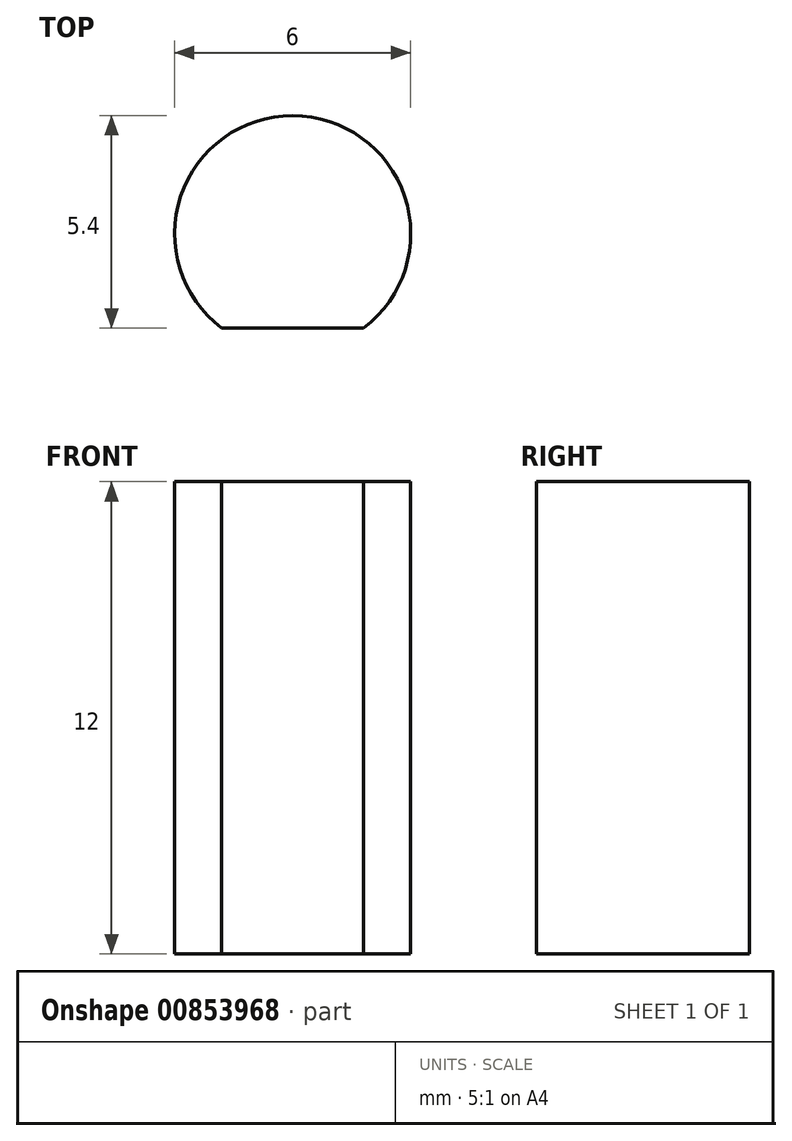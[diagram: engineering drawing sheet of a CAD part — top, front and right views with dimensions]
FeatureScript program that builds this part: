
annotation { "Feature Type Name" : "Feature", "Feature Type Description" : "" }
export const myFeature = defineFeature(function(context is Context, id is Id, definition is map)
    precondition{}
    {
        {
            var Q0;
            Q0=qCreatedBy(makeId("Top.planeOp"),FACE);
            var sketch = newSketch(context, id + "F0", { "sketchPlane" : qUnion([Q0])});
            skCircle(sketch, "E0", {"center": v(0, 0) * mm, "radius": 6.35 * mm});
            skSolve(sketch);
        }
        {
            var Q0;
            Q0=makeQuery(id+"F0.imprint","IMPRINT",FACE,{"disambiguationData":[TD([[makeQuery(id+"F0.imprint","IMPRINT",EDGE,{"derivedFrom":sQuery(id+"F0.wireOp",EDGE,"E0")}),1.0]])]});
            extrude(context, id + "F1", {"entities" : qUnion([Q0]), "depth" : 12 * mm, "offsetDistance" : 25 * mm});
        }
        {
            var Q0;
            Q0=makeQuery(id+"F1.opExtrude","CAP_FACE",FACE,{"disambiguationData":[OSD([sQuery(id+"F0.wireOp",EDGE,"E0")])],"isStart":false});
            var sketch = newSketch(context, id + "F2", { "sketchPlane" : qUnion([Q0])});
            skArc(sketch, "E1", {"start": v(-1.8, -2.4) * mm, "mid": v(0, 3) * mm, "end": v(1.8, -2.4) * mm});
            skLineSegment(sketch, "E2", {"start": v(-1.8, -2.4) * mm, "end": v(1.8, -2.4) * mm});
            skLineSegment(sketch, "E3", {"start": v(0, -2.4) * mm, "end": v(0, 3) * mm, "construction": true});
            skSolve(sketch);
        }
        {
            var Q0;
            Q0=makeQuery(id+"F2.imprint","IMPRINT",FACE,{"disambiguationData":[TD([[makeQuery(id+"F2.imprint","IMPRINT",EDGE,{"derivedFrom":sQuery(id+"F2.wireOp",EDGE,"E1")}),-1.0]])]});
            extrude(context, id + "F3", {"entities" : qUnion([Q0]), "operationType" : NewBodyOperationType.REMOVE, "endBound" : BoundingType.THROUGH_ALL, "oppositeDirection" : true, "depth" : 25 * mm, "offsetDistance" : 25 * mm});
        }
    });
